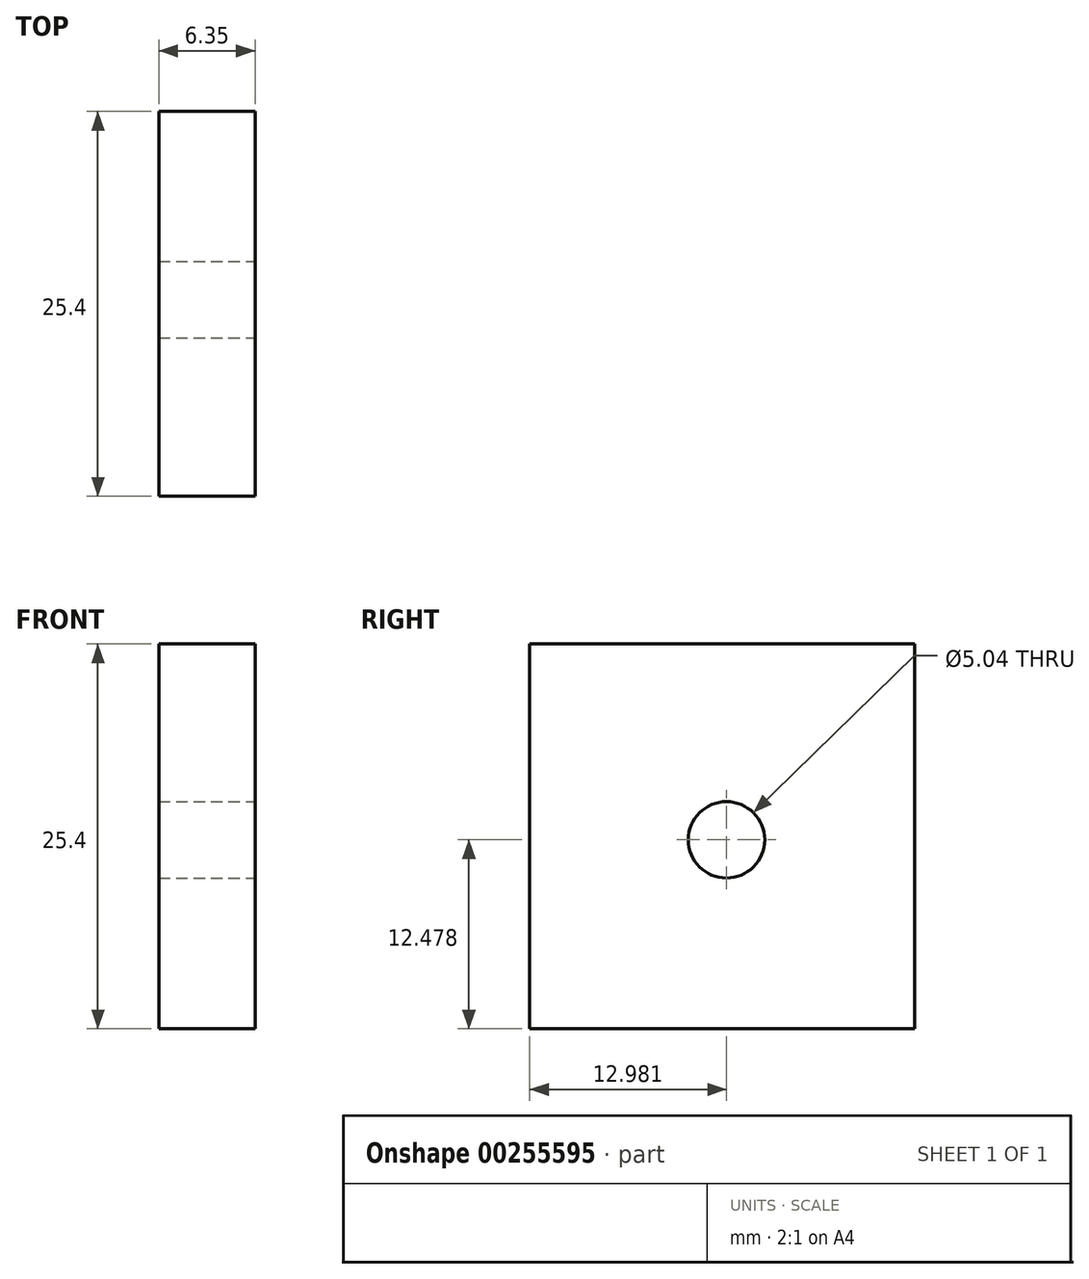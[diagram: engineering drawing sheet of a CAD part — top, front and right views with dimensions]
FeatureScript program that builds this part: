
annotation { "Feature Type Name" : "Feature", "Feature Type Description" : "" }
export const myFeature = defineFeature(function(context is Context, id is Id, definition is map)
    precondition{}
    {
        {
            var Q0;
            Q0=qCreatedBy(makeId("Right.planeOp"),FACE);
            var sketch = newSketch(context, id + "F0", { "sketchPlane" : qUnion([Q0])});
            skLineSegment(sketch, "E0.bottom", {"start": v(0, 0) * mm, "end": v(25.4, 0) * mm});
            skLineSegment(sketch, "E0.top", {"start": v(0, 25.4) * mm, "end": v(25.4, 25.4) * mm});
            skLineSegment(sketch, "E0.left", {"start": v(0, 0) * mm, "end": v(0, 25.4) * mm});
            skLineSegment(sketch, "E0.right", {"start": v(25.4, 0) * mm, "end": v(25.4, 25.4) * mm});
            skSolve(sketch);
        }
        {
            var Q0;
            Q0=makeQuery(id+"F0.imprint","IMPRINT",FACE,{"disambiguationData":[TD([[makeQuery(id+"F0.imprint","IMPRINT",EDGE,{"derivedFrom":sQuery(id+"F0.wireOp",EDGE,"E0.bottom")}),1.0]])]});
            extrude(context, id + "F1", {"entities" : qUnion([Q0]), "depth" : 6.35 * mm});
        }
        {
            var Q0;
            Q0=makeQuery(id+"F1.opExtrude","CAP_FACE",FACE,{"disambiguationData":[OSD([sQuery(id+"F0.wireOp",EDGE,"E0.bottom"),sQuery(id+"F0.wireOp",EDGE,"E0.top"),sQuery(id+"F0.wireOp",EDGE,"E0.left"),sQuery(id+"F0.wireOp",EDGE,"E0.right")])],"isStart":false});
            var sketch = newSketch(context, id + "F2", { "sketchPlane" : qUnion([Q0])});
            skCircle(sketch, "E1", {"center": v(12.98, 12.48) * mm, "radius": 2.52 * mm});
            skSolve(sketch);
        }
        {
            var Q0;
            Q0 = qSketchRegion(id + "F2", true);
            extrude(context, id + "F3", {"entities" : qUnion([Q0]), "operationType" : NewBodyOperationType.REMOVE, "oppositeDirection" : true, "depth" : 25.4 * mm});
        }
    });
